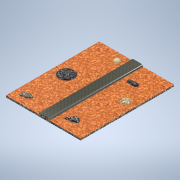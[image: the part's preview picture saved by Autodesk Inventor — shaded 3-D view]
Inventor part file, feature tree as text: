
AUTODESK INVENTOR PART (.ipt)
format: ipt  version: 2021 (Build 250183000, 183)  size: 275,968 bytes
history: native  units: mm
features: extrude x5, fillet x5, sketch x5
ambient origin geometry x8: Origin, YZ Plane, XZ Plane, XY Plane, X Axis, Y Axis, Z Axis, Center Point
bodies: Solid1 (feature_tree)
feature tree (15):
  extrude  "Extrusion1"  Depth=500.0mm
  extrude  "Extrusion2"  Depth=9.0mm TaperAngle=0.0deg
  fillet  "Fillet1"  Radius=10.0mm
  fillet  "Fillet2"  Radius=10.0mm
  extrude  "Extrusion3"  Depth=30.0mm
  fillet  "Fillet3"  Radius=15.0mm
  extrude  "Extrusion4"  Depth=5.0mm TaperAngle=0.0deg
  fillet  "Fillet4"  Radius=8.0mm
  extrude  "Extrusion5"  Depth=7.0mm TaperAngle=0.0deg
  fillet  "Fillet5"  Radius=5.0mm
  sketch  "Sketch1"  dims[d0=400.0mm d1=500.0mm]
  sketch  "Sketch2"  dims[d2=10.0mm d3=0.0mm d4=9.0mm d5=0.0mm d6=10.0mm d7=10.0mm]
  sketch  "Sketch3"  dims[d8=80.0mm d9=30.0mm d10=15.0mm]
  sketch  "Sketch4"  dims[d11=15.0mm d12=5.0mm d13=0.0mm d14=8.0mm]
  sketch  "Sketch5"  dims[d15=12.0mm d16=7.0mm d17=0.0mm d18=5.0mm d19=12.0mm d20=7.0mm d21=0.0mm d22=5.0mm]
